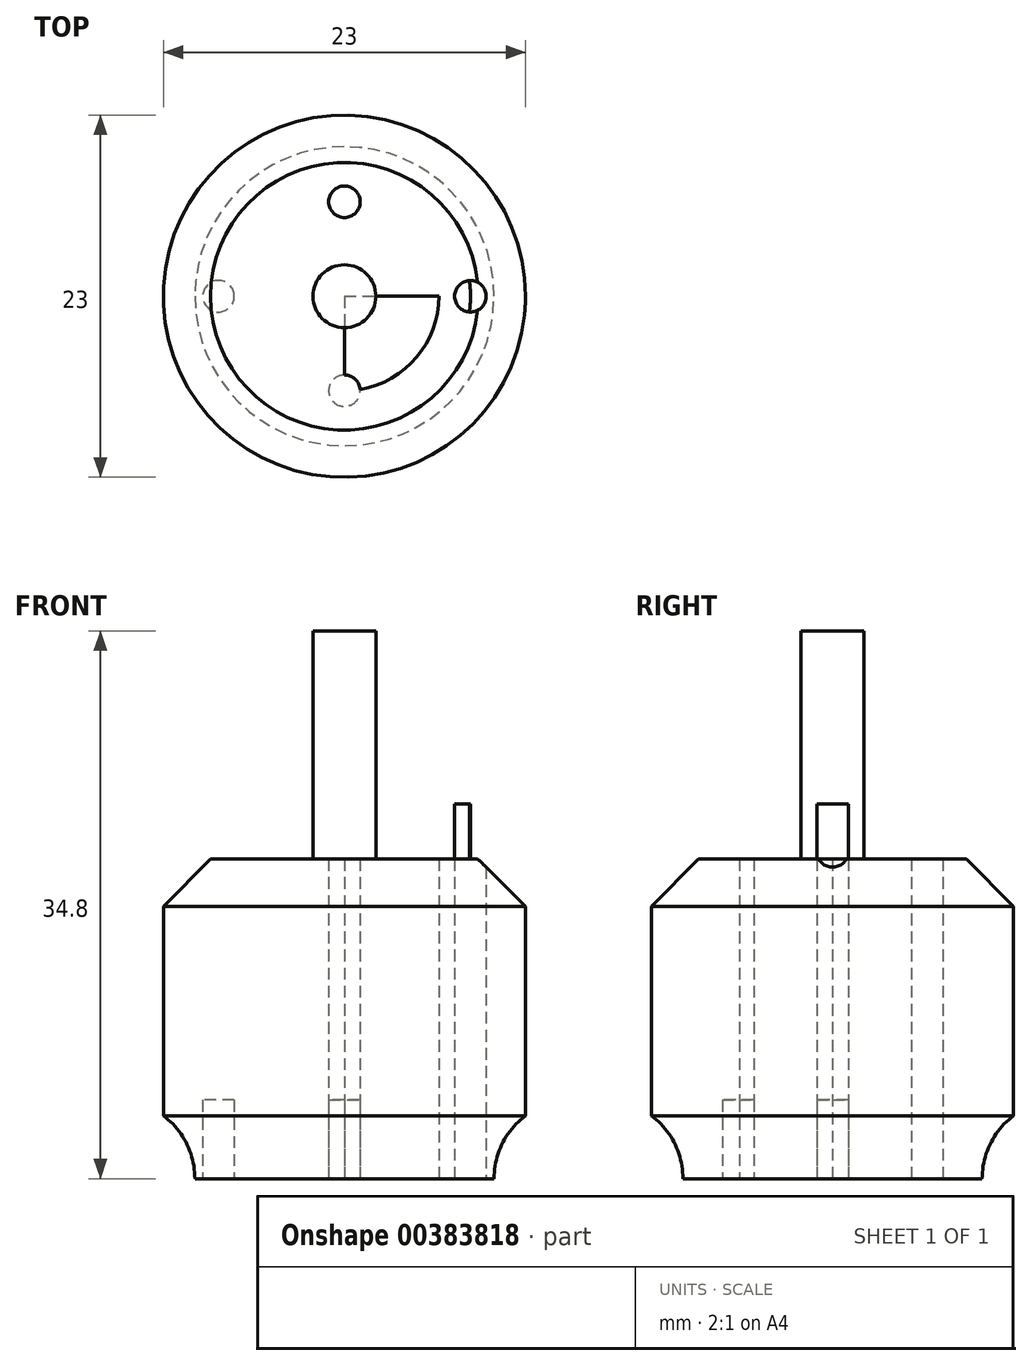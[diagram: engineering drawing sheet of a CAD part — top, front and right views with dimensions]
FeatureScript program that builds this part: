
annotation { "Feature Type Name" : "Feature", "Feature Type Description" : "" }
export const myFeature = defineFeature(function(context is Context, id is Id, definition is map)
    precondition{}
    {
        {
            var Q0;
            Q0=qCreatedBy(makeId("Top.planeOp"),FACE);
            var sketch = newSketch(context, id + "F0", { "sketchPlane" : qUnion([Q0])});
            skCircle(sketch, "E0", {"center": v(0, 0) * mm, "radius": 11.5 * mm});
            skCircle(sketch, "E1", {"center": v(0, 0) * mm, "radius": 8 * mm});
            skCircle(sketch, "E2", {"center": v(0, 0) * mm, "radius": 6 * mm});
            skLineSegment(sketch, "E3", {"start": v(0, 0) * mm, "end": v(8, 0) * mm});
            skLineSegment(sketch, "E4", {"start": v(8, 0) * mm, "end": v(-8, 0) * mm});
            skLineSegment(sketch, "E5", {"start": v(0, 0) * mm, "end": v(0, 6) * mm});
            skLineSegment(sketch, "E6", {"start": v(0, 6) * mm, "end": v(0, -6) * mm});
            skCircle(sketch, "E7", {"center": v(0, 6) * mm, "radius": 1 * mm});
            skCircle(sketch, "E8", {"center": v(8, 0) * mm, "radius": 1 * mm});
            skCircle(sketch, "E9", {"center": v(0, -6) * mm, "radius": 1 * mm});
            skCircle(sketch, "E10", {"center": v(-8, 0) * mm, "radius": 1 * mm});
            skSolve(sketch);
        }
        {
            var Q0;
            Q0 = qSketchRegion(id + "F0", true);
            var Q1;
            {var subQ0=sQuery(id+"F0.wireOp",EDGE,"E1");var subQ1=makeQuery(id+"F0.imprint","INTERSECT",VERTEX,{"disambiguationData":[OD(0.0)],"derivedFrom":[subQ0,sQuery(id+"F0.wireOp",EDGE,"E4")]});Q1=makeQuery(id+"F0.imprint","IMPRINT",FACE,{"disambiguationData":[TD([[makeQuery(id+"F0.imprint","IMPRINT",EDGE,{"disambiguationData":[TD([[subQ1,-1.0]])],"derivedFrom":subQ0}),-1.0]])]});}
            var Q2;
            {var subQ3=sQuery(id+"F0.wireOp",EDGE,"E8");var subQ9=sQuery(id+"F0.wireOp",EDGE,"E1");var subQ10=makeQuery(id+"F0.imprint","INTERSECT",VERTEX,{"disambiguationData":[OD(0.0)],"derivedFrom":[subQ9,subQ3]});Q2=makeQuery(id+"F0.imprint","IMPRINT",FACE,{"disambiguationData":[TD([[makeQuery(id+"F0.imprint","IMPRINT",EDGE,{"disambiguationData":[TD([[subQ10,-1.0]])],"derivedFrom":subQ9}),1.0]])]});}
            var Q3;
            {var subQ0=sQuery(id+"F0.wireOp",EDGE,"E7");var subQ1=sQuery(id+"F0.wireOp",EDGE,"E2");var subQ2=makeQuery(id+"F0.imprint","INTERSECT",VERTEX,{"disambiguationData":[OD(0.0)],"derivedFrom":[subQ1,subQ0]});Q3=makeQuery(id+"F0.imprint","IMPRINT",FACE,{"disambiguationData":[TD([[makeQuery(id+"F0.imprint","IMPRINT",EDGE,{"disambiguationData":[TD([[subQ2,1.0]])],"derivedFrom":subQ1}),1.0]])]});}
            var Q4;
            {var subQ0=sQuery(id+"F0.wireOp",EDGE,"E7");var subQ1=sQuery(id+"F0.wireOp",EDGE,"E2");var subQ2=makeQuery(id+"F0.imprint","INTERSECT",VERTEX,{"disambiguationData":[OD(1.0)],"derivedFrom":[subQ1,subQ0]});Q4=makeQuery(id+"F0.imprint","IMPRINT",FACE,{"disambiguationData":[TD([[makeQuery(id+"F0.imprint","IMPRINT",EDGE,{"disambiguationData":[TD([[subQ2,-1.0]])],"derivedFrom":subQ1}),1.0]])]});}
            var Q5;
            {var subQ0=sQuery(id+"F0.wireOp",EDGE,"E4");var subQ1=sQuery(id+"F0.wireOp",EDGE,"E2");var subQ2=makeQuery(id+"F0.imprint","INTERSECT",VERTEX,{"disambiguationData":[OD(1.0)],"derivedFrom":[subQ1,subQ0]});Q5=makeQuery(id+"F0.imprint","IMPRINT",FACE,{"disambiguationData":[TD([[makeQuery(id+"F0.imprint","IMPRINT",EDGE,{"disambiguationData":[TD([[subQ2,-1.0]])],"derivedFrom":subQ1}),1.0]])]});}
            var Q6;
            {var subQ0=sQuery(id+"F0.wireOp",EDGE,"E4");var subQ1=sQuery(id+"F0.wireOp",EDGE,"E2");var subQ2=makeQuery(id+"F0.imprint","INTERSECT",VERTEX,{"disambiguationData":[OD(0.0)],"derivedFrom":[subQ1,subQ0]});Q6=makeQuery(id+"F0.imprint","IMPRINT",FACE,{"disambiguationData":[TD([[makeQuery(id+"F0.imprint","IMPRINT",EDGE,{"disambiguationData":[TD([[subQ2,1.0]])],"derivedFrom":subQ1}),1.0]])]});}
            var Q7;
            {var subQ0=sQuery(id+"F0.wireOp",EDGE,"E6");var subQ1=sQuery(id+"F0.wireOp",EDGE,"E2");var subQ2=makeQuery(id+"F0.imprint","INTERSECT",VERTEX,{"disambiguationData":[OD(0.0)],"derivedFrom":[subQ1,subQ0]});Q7=makeQuery(id+"F0.imprint","IMPRINT",FACE,{"disambiguationData":[TD([[makeQuery(id+"F0.imprint","IMPRINT",EDGE,{"disambiguationData":[TD([[subQ2,1.0]])],"derivedFrom":subQ1}),1.0]])]});}
            var Q8;
            {var subQ0=sQuery(id+"F0.wireOp",EDGE,"E6");var subQ1=sQuery(id+"F0.wireOp",EDGE,"E2");var subQ2=makeQuery(id+"F0.imprint","INTERSECT",VERTEX,{"disambiguationData":[OD(0.0)],"derivedFrom":[subQ1,subQ0]});Q8=makeQuery(id+"F0.imprint","IMPRINT",FACE,{"disambiguationData":[TD([[makeQuery(id+"F0.imprint","IMPRINT",EDGE,{"disambiguationData":[TD([[subQ2,-1.0]])],"derivedFrom":subQ1}),1.0]])]});}
            var Q9;
            {var subQ0=sQuery(id+"F0.wireOp",EDGE,"E2");var subQ1=makeQuery(id+"F0.imprint","INTERSECT",VERTEX,{"disambiguationData":[OD(0.0)],"derivedFrom":[subQ0,sQuery(id+"F0.wireOp",EDGE,"E6")]});Q9=makeQuery(id+"F0.imprint","IMPRINT",FACE,{"disambiguationData":[TD([[makeQuery(id+"F0.imprint","IMPRINT",EDGE,{"disambiguationData":[TD([[subQ1,1.0]])],"derivedFrom":subQ0}),-1.0]])]});}
            var Q10;
            {var subQ0=sQuery(id+"F0.wireOp",EDGE,"E4");var subQ1=sQuery(id+"F0.wireOp",EDGE,"E1");var subQ2=makeQuery(id+"F0.imprint","INTERSECT",VERTEX,{"disambiguationData":[OD(0.0)],"derivedFrom":[subQ1,subQ0]});Q10=makeQuery(id+"F0.imprint","IMPRINT",FACE,{"disambiguationData":[TD([[makeQuery(id+"F0.imprint","IMPRINT",EDGE,{"disambiguationData":[TD([[subQ2,1.0]])],"derivedFrom":subQ1}),1.0]])]});}
            var Q11;
            {var subQ0=sQuery(id+"F0.wireOp",EDGE,"E4");var subQ1=sQuery(id+"F0.wireOp",EDGE,"E1");var subQ2=makeQuery(id+"F0.imprint","INTERSECT",VERTEX,{"disambiguationData":[OD(0.0)],"derivedFrom":[subQ1,subQ0]});Q11=makeQuery(id+"F0.imprint","IMPRINT",FACE,{"disambiguationData":[TD([[makeQuery(id+"F0.imprint","IMPRINT",EDGE,{"disambiguationData":[TD([[subQ2,-1.0]])],"derivedFrom":subQ1}),1.0]])]});}
            var Q12;
            {var subQ5=sQuery(id+"F0.wireOp",EDGE,"E10");var subQ6=sQuery(id+"F0.wireOp",EDGE,"E1");var subQ7=makeQuery(id+"F0.imprint","INTERSECT",VERTEX,{"disambiguationData":[OD(1.0)],"derivedFrom":[subQ6,subQ5]});Q12=makeQuery(id+"F0.imprint","IMPRINT",FACE,{"disambiguationData":[TD([[makeQuery(id+"F0.imprint","IMPRINT",EDGE,{"disambiguationData":[TD([[subQ7,-1.0]])],"derivedFrom":subQ6}),1.0]])]});}
            var Q13;
            {var subQ0=sQuery(id+"F0.wireOp",EDGE,"E2");var subQ1=makeQuery(id+"F0.imprint","INTERSECT",VERTEX,{"disambiguationData":[OD(1.0)],"derivedFrom":[subQ0,sQuery(id+"F0.wireOp",EDGE,"E6")]});Q13=makeQuery(id+"F0.imprint","IMPRINT",FACE,{"disambiguationData":[TD([[makeQuery(id+"F0.imprint","IMPRINT",EDGE,{"disambiguationData":[TD([[subQ1,1.0]])],"derivedFrom":subQ0}),-1.0]])]});}
            var Q14;
            {var subQ0=sQuery(id+"F0.wireOp",EDGE,"E6");var subQ1=sQuery(id+"F0.wireOp",EDGE,"E2");var subQ2=makeQuery(id+"F0.imprint","INTERSECT",VERTEX,{"disambiguationData":[OD(1.0)],"derivedFrom":[subQ1,subQ0]});Q14=makeQuery(id+"F0.imprint","IMPRINT",FACE,{"disambiguationData":[TD([[makeQuery(id+"F0.imprint","IMPRINT",EDGE,{"disambiguationData":[TD([[subQ2,-1.0]])],"derivedFrom":subQ1}),1.0]])]});}
            var Q15;
            {var subQ0=sQuery(id+"F0.wireOp",EDGE,"E6");var subQ1=sQuery(id+"F0.wireOp",EDGE,"E2");var subQ2=makeQuery(id+"F0.imprint","INTERSECT",VERTEX,{"disambiguationData":[OD(1.0)],"derivedFrom":[subQ1,subQ0]});Q15=makeQuery(id+"F0.imprint","IMPRINT",FACE,{"disambiguationData":[TD([[makeQuery(id+"F0.imprint","IMPRINT",EDGE,{"disambiguationData":[TD([[subQ2,1.0]])],"derivedFrom":subQ1}),1.0]])]});}
            var Q16;
            {var subQ0=sQuery(id+"F0.wireOp",EDGE,"E4");var subQ1=sQuery(id+"F0.wireOp",EDGE,"E1");var subQ2=makeQuery(id+"F0.imprint","INTERSECT",VERTEX,{"disambiguationData":[OD(1.0)],"derivedFrom":[subQ1,subQ0]});Q16=makeQuery(id+"F0.imprint","IMPRINT",FACE,{"disambiguationData":[TD([[makeQuery(id+"F0.imprint","IMPRINT",EDGE,{"disambiguationData":[TD([[subQ2,-1.0]])],"derivedFrom":subQ1}),1.0]])]});}
            var Q17;
            {var subQ0=sQuery(id+"F0.wireOp",EDGE,"E1");var subQ1=makeQuery(id+"F0.imprint","INTERSECT",VERTEX,{"disambiguationData":[OD(1.0)],"derivedFrom":[subQ0,sQuery(id+"F0.wireOp",EDGE,"E4")]});Q17=makeQuery(id+"F0.imprint","IMPRINT",FACE,{"disambiguationData":[TD([[makeQuery(id+"F0.imprint","IMPRINT",EDGE,{"disambiguationData":[TD([[subQ1,1.0]])],"derivedFrom":subQ0}),-1.0]])]});}
            var Q18;
            {var subQ0=sQuery(id+"F0.wireOp",EDGE,"E4");var subQ1=sQuery(id+"F0.wireOp",EDGE,"E1");var subQ2=makeQuery(id+"F0.imprint","INTERSECT",VERTEX,{"disambiguationData":[OD(1.0)],"derivedFrom":[subQ1,subQ0]});Q18=makeQuery(id+"F0.imprint","IMPRINT",FACE,{"disambiguationData":[TD([[makeQuery(id+"F0.imprint","IMPRINT",EDGE,{"disambiguationData":[TD([[subQ2,1.0]])],"derivedFrom":subQ1}),1.0]])]});}
            extrude(context, id + "F1", {"entities" : qUnion([Q0, Q1, Q2, Q3, Q4, Q5, Q6, Q7, Q8, Q9, Q10, Q11, Q12, Q13, Q14, Q15, Q16, Q17, Q18]), "depth" : 20.3 * mm});
        }
        {
            var Q0;
            Q0=makeQuery(id+"F1.opExtrude","CAP_FACE",FACE,{"disambiguationData":[OSD([sQuery(id+"F0.wireOp",EDGE,"E0"),sQuery(id+"F0.wireOp",EDGE,"E7"),sQuery(id+"F0.wireOp",EDGE,"E8"),sQuery(id+"F0.wireOp",EDGE,"E9"),sQuery(id+"F0.wireOp",EDGE,"E10")])],"isStart":true});
            var sketch = newSketch(context, id + "F2", { "sketchPlane" : qUnion([Q0])});
            skCircle(sketch, "E11", {"center": v(0, 0) * mm, "radius": 9.5 * mm});
            skCircle(sketch, "E12", {"center": v(0, 0) * mm, "radius": 11.5 * mm});
            skSolve(sketch);
        }
        {
            var Q0;
            Q0 = qSketchRegion(id + "F2", true);
            extrude(context, id + "F3", {"entities" : qUnion([Q0]), "operationType" : NewBodyOperationType.REMOVE, "oppositeDirection" : true, "depth" : 4 * mm});
        }
        {
            var Q0;
            Q0=makeQuery(id+"F3.boolean.opBoolean","COPY",EDGE,{"derivedFrom":makeQuery(id+"F3.opExtrude","CAP_EDGE",EDGE,{"disambiguationData":[OSD([sQuery(id+"F2.wireOp",EDGE,"E11")])],"isStart":false})});
            fillet(context, id + "F4", {"entities" : qUnion([Q0]), "radius" : 5 * mm, "tangentPropagation" : true, "allowEdgeOverflow" : false});
        }
        {
            var Q0;
            {var subQ0=sQuery(id+"F0.wireOp",EDGE,"E1");var subQ1=makeQuery(id+"F0.imprint","INTERSECT",VERTEX,{"disambiguationData":[OD(1.0)],"derivedFrom":[subQ0,sQuery(id+"F0.wireOp",EDGE,"E4")]});Q0=makeQuery(id+"F0.imprint","IMPRINT",FACE,{"disambiguationData":[TD([[makeQuery(id+"F0.imprint","IMPRINT",EDGE,{"disambiguationData":[TD([[subQ1,1.0]])],"derivedFrom":subQ0}),-1.0]])]});}
            var Q1;
            {var subQ0=sQuery(id+"F0.wireOp",EDGE,"E4");var subQ1=sQuery(id+"F0.wireOp",EDGE,"E1");var subQ2=makeQuery(id+"F0.imprint","INTERSECT",VERTEX,{"disambiguationData":[OD(1.0)],"derivedFrom":[subQ1,subQ0]});Q1=makeQuery(id+"F0.imprint","IMPRINT",FACE,{"disambiguationData":[TD([[makeQuery(id+"F0.imprint","IMPRINT",EDGE,{"disambiguationData":[TD([[subQ2,-1.0]])],"derivedFrom":subQ1}),1.0]])]});}
            var Q2;
            {var subQ0=sQuery(id+"F0.wireOp",EDGE,"E4");var subQ1=sQuery(id+"F0.wireOp",EDGE,"E1");var subQ2=makeQuery(id+"F0.imprint","INTERSECT",VERTEX,{"disambiguationData":[OD(1.0)],"derivedFrom":[subQ1,subQ0]});Q2=makeQuery(id+"F0.imprint","IMPRINT",FACE,{"disambiguationData":[TD([[makeQuery(id+"F0.imprint","IMPRINT",EDGE,{"disambiguationData":[TD([[subQ2,1.0]])],"derivedFrom":subQ1}),1.0]])]});}
            var Q3;
            {var subQ0=sQuery(id+"F0.wireOp",EDGE,"E2");var subQ1=makeQuery(id+"F0.imprint","INTERSECT",VERTEX,{"disambiguationData":[OD(0.0)],"derivedFrom":[subQ0,sQuery(id+"F0.wireOp",EDGE,"E6")]});Q3=makeQuery(id+"F0.imprint","IMPRINT",FACE,{"disambiguationData":[TD([[makeQuery(id+"F0.imprint","IMPRINT",EDGE,{"disambiguationData":[TD([[subQ1,1.0]])],"derivedFrom":subQ0}),-1.0]])]});}
            var Q4;
            {var subQ0=sQuery(id+"F0.wireOp",EDGE,"E6");var subQ1=sQuery(id+"F0.wireOp",EDGE,"E2");var subQ2=makeQuery(id+"F0.imprint","INTERSECT",VERTEX,{"disambiguationData":[OD(0.0)],"derivedFrom":[subQ1,subQ0]});Q4=makeQuery(id+"F0.imprint","IMPRINT",FACE,{"disambiguationData":[TD([[makeQuery(id+"F0.imprint","IMPRINT",EDGE,{"disambiguationData":[TD([[subQ2,1.0]])],"derivedFrom":subQ1}),1.0]])]});}
            var Q5;
            {var subQ0=sQuery(id+"F0.wireOp",EDGE,"E6");var subQ1=sQuery(id+"F0.wireOp",EDGE,"E2");var subQ2=makeQuery(id+"F0.imprint","INTERSECT",VERTEX,{"disambiguationData":[OD(0.0)],"derivedFrom":[subQ1,subQ0]});Q5=makeQuery(id+"F0.imprint","IMPRINT",FACE,{"disambiguationData":[TD([[makeQuery(id+"F0.imprint","IMPRINT",EDGE,{"disambiguationData":[TD([[subQ2,-1.0]])],"derivedFrom":subQ1}),1.0]])]});}
            var Q6;
            {var subQ0=sQuery(id+"F0.wireOp",EDGE,"E1");var subQ1=makeQuery(id+"F0.imprint","INTERSECT",VERTEX,{"disambiguationData":[OD(0.0)],"derivedFrom":[subQ0,sQuery(id+"F0.wireOp",EDGE,"E4")]});Q6=makeQuery(id+"F0.imprint","IMPRINT",FACE,{"disambiguationData":[TD([[makeQuery(id+"F0.imprint","IMPRINT",EDGE,{"disambiguationData":[TD([[subQ1,-1.0]])],"derivedFrom":subQ0}),-1.0]])]});}
            var Q7;
            {var subQ0=sQuery(id+"F0.wireOp",EDGE,"E4");var subQ1=sQuery(id+"F0.wireOp",EDGE,"E1");var subQ2=makeQuery(id+"F0.imprint","INTERSECT",VERTEX,{"disambiguationData":[OD(0.0)],"derivedFrom":[subQ1,subQ0]});Q7=makeQuery(id+"F0.imprint","IMPRINT",FACE,{"disambiguationData":[TD([[makeQuery(id+"F0.imprint","IMPRINT",EDGE,{"disambiguationData":[TD([[subQ2,1.0]])],"derivedFrom":subQ1}),1.0]])]});}
            var Q8;
            {var subQ0=sQuery(id+"F0.wireOp",EDGE,"E4");var subQ1=sQuery(id+"F0.wireOp",EDGE,"E1");var subQ2=makeQuery(id+"F0.imprint","INTERSECT",VERTEX,{"disambiguationData":[OD(0.0)],"derivedFrom":[subQ1,subQ0]});Q8=makeQuery(id+"F0.imprint","IMPRINT",FACE,{"disambiguationData":[TD([[makeQuery(id+"F0.imprint","IMPRINT",EDGE,{"disambiguationData":[TD([[subQ2,-1.0]])],"derivedFrom":subQ1}),1.0]])]});}
            var Q9;
            {var subQ0=sQuery(id+"F0.wireOp",EDGE,"E2");var subQ1=makeQuery(id+"F0.imprint","INTERSECT",VERTEX,{"disambiguationData":[OD(1.0)],"derivedFrom":[subQ0,sQuery(id+"F0.wireOp",EDGE,"E6")]});Q9=makeQuery(id+"F0.imprint","IMPRINT",FACE,{"disambiguationData":[TD([[makeQuery(id+"F0.imprint","IMPRINT",EDGE,{"disambiguationData":[TD([[subQ1,1.0]])],"derivedFrom":subQ0}),-1.0]])]});}
            var Q10;
            {var subQ0=sQuery(id+"F0.wireOp",EDGE,"E6");var subQ1=sQuery(id+"F0.wireOp",EDGE,"E2");var subQ2=makeQuery(id+"F0.imprint","INTERSECT",VERTEX,{"disambiguationData":[OD(1.0)],"derivedFrom":[subQ1,subQ0]});Q10=makeQuery(id+"F0.imprint","IMPRINT",FACE,{"disambiguationData":[TD([[makeQuery(id+"F0.imprint","IMPRINT",EDGE,{"disambiguationData":[TD([[subQ2,1.0]])],"derivedFrom":subQ1}),1.0]])]});}
            var Q11;
            {var subQ0=sQuery(id+"F0.wireOp",EDGE,"E6");var subQ1=sQuery(id+"F0.wireOp",EDGE,"E2");var subQ2=makeQuery(id+"F0.imprint","INTERSECT",VERTEX,{"disambiguationData":[OD(1.0)],"derivedFrom":[subQ1,subQ0]});Q11=makeQuery(id+"F0.imprint","IMPRINT",FACE,{"disambiguationData":[TD([[makeQuery(id+"F0.imprint","IMPRINT",EDGE,{"disambiguationData":[TD([[subQ2,-1.0]])],"derivedFrom":subQ1}),1.0]])]});}
            extrude(context, id + "F5", {"entities" : qUnion([Q0, Q1, Q2, Q3, Q4, Q5, Q6, Q7, Q8, Q9, Q10, Q11]), "operationType" : NewBodyOperationType.REMOVE, "depth" : 5 * mm});
        }
        {
            var Q0;
            Q0=makeQuery(id+"F1.opExtrude","CAP_EDGE",EDGE,{"disambiguationData":[OSD([sQuery(id+"F0.wireOp",EDGE,"E0")])],"isStart":false});
            chamfer(context, id + "F6", {"entities" : qUnion([Q0]), "width" : 3 * mm, "tangentPropagation" : true});
        }
        {
            var Q0;
            Q0=makeQuery(id+"F1.opExtrude","CAP_FACE",FACE,{"disambiguationData":[OSD([sQuery(id+"F0.wireOp",EDGE,"E0")])],"isStart":false});
            var sketch = newSketch(context, id + "F7", { "sketchPlane" : qUnion([Q0])});
            skCircle(sketch, "E13", {"center": v(0, 0) * mm, "radius": 8 * mm});
            skCircle(sketch, "E14", {"center": v(0, 0) * mm, "radius": 2 * mm});
            skSolve(sketch);
        }
        {
            var Q0;
            Q0=makeQuery(id+"F7.imprint","IMPRINT",FACE,{"disambiguationData":[TD([[makeQuery(id+"F7.imprint","IMPRINT",EDGE,{"derivedFrom":sQuery(id+"F7.wireOp",EDGE,"E14")}),1.0]])]});
            extrude(context, id + "F8", {"entities" : qUnion([Q0]), "operationType" : NewBodyOperationType.ADD, "depth" : 14.5 * mm});
        }
        {
            var Q0;
            Q0=makeQuery(id+"F7.imprint","IMPRINT",FACE,{"disambiguationData":[TD([[makeQuery(id+"F7.imprint","IMPRINT",EDGE,{"derivedFrom":sQuery(id+"F7.wireOp",EDGE,"E13")}),1.0]])]});
            extrude(context, id + "F9", {"entities" : qUnion([Q0]), "operationType" : NewBodyOperationType.ADD, "depth" : 3.5 * mm});
        }
    });
